# Revit family: 500_Slenderline_Sliding_Window_XXXX_Standard
name_source: partatom
category: Windows
revit_build: Autodesk Revit 2014 (Build: 20130308_1515(x64)
units: mm (PartAtom-declared; Revit-internal decimal feet)

## types (78) — shared parameters
Astragal Sash Gap = 1 mm  [stored 0.00328084 ft]
Centered In Wall = Yes
Custom Sash Width Side = 800 mm  [stored 2.62467 ft]
Default Sill Height = 800 mm  [stored 2.62467 ft]
Description = Slenderline Sliding Window
Equal Sash Width = Yes
Frame Thickness = 54 mm
Heavy Duty Handle = No
Heavy Duty Handle Gap = 27 mm
Heavy Duty Interlocker = No
Limit Sash Height Max = 1500 mm  [stored 4.92126 ft]
Limit Sash Height Min = 300 mm  [stored 0.984252 ft]
Limit Sash Width Max = 750 mm  [stored 2.46063 ft]
Limit Sash Width Min = 300 mm  [stored 0.984252 ft]
Limit Window Height Max = 1575 mm
Limit Window Height Min = 375 mm
Limit Window Width Max = 3024 mm
Limit Window Width Min = 1224 mm
Manufacturer = Crealco
Model = 500
Sash Frame Seal = 1 mm  [stored 0.00328084 ft]
Sash Rail Fore Aft Spacing = 2 mm  [stored 0.00656168 ft]
Standard Interlocker = Yes
URL = www.crealco.co.za
Wall Closure = By host
zero-valued in all types: Custom Frame Offset From Exterior, Is Heavy Duty Handle, Is Heavy Duty Mullion

## per-type parameters (varying)
| type | Area Middle Sash Glazing | Area Side Sash Glazing | Clearvue SHGC Value | Clearvue U Value | Custom Windload | Custom Window Height | Custom Window Width | Energy Advantage SHGC Value | Energy Advantage U Value | Height | Intruderprufe LowE SHGC Value | Intruderprufe LowE U Value | Intruderprufe SHGC Value | Intruderprufe U Value | Limit Sash Width Side Max | Limit Sash Width Side Min | Max Pane Area | Sash Height | Sash Width Middle | Sash Width Sides | Width | Windload Design |
| 500SW-1206XXXX-1000Pa | 0.12 m² | 0.12 m² | 0.535 | 5.67 | 1000 mm  [stored 3.28084 ft] | 590 mm  [stored 1.9357 ft] | 1190 mm  [stored 3.9042 ft] | 0.479 | 4.55 | 590 mm  [stored 1.9357 ft] | 0.406 | 4.29 | 0.508 | 5.53 | 300 mm  [stored 0.984252 ft] | 300 mm  [stored 0.984252 ft] | 0.12 m² | 515 mm | 300 mm  [stored 0.984252 ft] | 300 mm  [stored 0.984252 ft] | 1224 mm | 1000 mm  [stored 3.28084 ft] |
| 500SW-1506XXXX-1000Pa | 0.15 m² | 0.15 m² | 0.522 | 5.78 | 1000 mm  [stored 3.28084 ft] | 590 mm  [stored 1.9357 ft] | 1490 mm  [stored 4.88845 ft] | 0.495 | 4.57 | 590 mm  [stored 1.9357 ft] | 0.419 | 4.38 | 0.524 | 5.65 | 433 mm | 300 mm  [stored 0.984252 ft] | 0.15 m² | 515 mm | 367 mm | 367 mm | 1490 mm  [stored 4.88845 ft] | 1000 mm  [stored 3.28084 ft] |
| 500SW-1806XXXX-1000Pa | 0.18 m² | 0.18 m² | 0.564 | 5.86 | 1000 mm  [stored 3.28084 ft] | 590 mm  [stored 1.9357 ft] | 1790 mm  [stored 5.8727 ft] | 0.506 | 4.59 | 590 mm  [stored 1.9357 ft] | 0.429 | 4.43 | 0.536 | 5.72 | 583 mm | 300 mm  [stored 0.984252 ft] | 0.18 m² | 515 mm | 442 mm | 442 mm | 1790 mm  [stored 5.8727 ft] | 1000 mm  [stored 3.28084 ft] |
| 500SW-2106XXXX-1000Pa | 0.22 m² | 0.22 m² | 0.573 | 5.91 | 1000 mm  [stored 3.28084 ft] | 590 mm  [stored 1.9357 ft] | 2090 mm  [stored 6.85696 ft] | 0.513 | 4.61 | 590 mm  [stored 1.9357 ft] | 0.435 | 4.48 | 0.544 | 5.78 | 733 mm | 300 mm  [stored 0.984252 ft] | 0.22 m² | 515 mm | 517 mm | 517 mm | 2090 mm  [stored 6.85696 ft] | 1000 mm  [stored 3.28084 ft] |
| 500SW-2406XXXX-1000Pa | 0.25 m² | 0.25 m² | 0.579 | 5.95 | 1000 mm  [stored 3.28084 ft] | 590 mm  [stored 1.9357 ft] | 2390 mm  [stored 7.84121 ft] | 0.519 | 4.61 | 590 mm  [stored 1.9357 ft] | 0.44 | 4.51 | 0.55 | 5.82 | 750 mm  [stored 2.46063 ft] | 433 mm | 0.25 m² | 515 mm | 592 mm | 592 mm | 2390 mm  [stored 7.84121 ft] | 1000 mm  [stored 3.28084 ft] |
| 500SW-2706XXXX-1000Pa | 0.28 m² | 0.28 m² | 0.584 | 5.99 | 1000 mm  [stored 3.28084 ft] | 590 mm  [stored 1.9357 ft] | 2690 mm  [stored 8.82546 ft] | 0.523 | 4.62 | 590 mm  [stored 1.9357 ft] | 0.443 | 4.53 | 0.554 | 5.85 | 750 mm  [stored 2.46063 ft] | 583 mm | 0.28 m² | 515 mm | 667 mm | 667 mm | 2690 mm  [stored 8.82546 ft] | 1000 mm  [stored 3.28084 ft] |
| 500SW-3006XXXX-1000Pa | 0.32 m² | 0.32 m² | 0.588 | 6.01 | 1000 mm  [stored 3.28084 ft] | 590 mm  [stored 1.9357 ft] | 2990 mm  [stored 9.80971 ft] | 0.527 | 4.63 | 590 mm  [stored 1.9357 ft] | 0.47 | 4.56 | 0.588 | 5.88 | 750 mm  [stored 2.46063 ft] | 733 mm | 0.32 m² | 515 mm | 742 mm | 742 mm | 2990 mm  [stored 9.80971 ft] | 1000 mm  [stored 3.28084 ft] |
| 500SW-1209XXXX-1000Pa | 0.2 m² | 0.2 m² | 0.6 | 5.59 | 1000 mm  [stored 3.28084 ft] | 890 mm  [stored 2.91995 ft] | 1190 mm  [stored 3.9042 ft] | 0.538 | 4.33 | 890 mm  [stored 2.91995 ft] | 0.456 | 4.22 | 0.57 | 5.44 | 300 mm  [stored 0.984252 ft] | 300 mm  [stored 0.984252 ft] | 0.2 m² | 815 mm | 300 mm  [stored 0.984252 ft] | 300 mm  [stored 0.984252 ft] | 1224 mm | 1000 mm  [stored 3.28084 ft] |
| 500SW-1509XXXX-1000Pa | 0.25 m² | 0.25 m² | 0.62 | 5.69 | 1000 mm  [stored 3.28084 ft] | 890 mm  [stored 2.91995 ft] | 1490 mm  [stored 4.88845 ft] | 0.555 | 4.33 | 890 mm  [stored 2.91995 ft] | 0.471 | 4.3 | 0.589 | 5.55 | 433 mm | 300 mm  [stored 0.984252 ft] | 0.25 m² | 815 mm | 367 mm | 367 mm | 1490 mm  [stored 4.88845 ft] | 1000 mm  [stored 3.28084 ft] |
| 500SW-1809XXXX-1000Pa | 0.31 m² | 0.31 m² | 0.634 | 5.76 | 1000 mm  [stored 3.28084 ft] | 890 mm  [stored 2.91995 ft] | 1790 mm  [stored 5.8727 ft] | 0.567 | 4.33 | 890 mm  [stored 2.91995 ft] | 0.481 | 4.36 | 0.601 | 5.63 | 583 mm | 300 mm  [stored 0.984252 ft] | 0.31 m² | 815 mm | 442 mm | 442 mm | 1790 mm  [stored 5.8727 ft] | 1000 mm  [stored 3.28084 ft] |
| 500SW-2109XXXX-1000Pa | 0.36 m² | 0.36 m² | 0.643 | 5.81 | 1000 mm  [stored 3.28084 ft] | 890 mm  [stored 2.91995 ft] | 2090 mm  [stored 6.85696 ft] | 0.576 | 4.34 | 890 mm  [stored 2.91995 ft] | 0.488 | 4.4 | 0.61 | 5.68 | 733 mm | 300 mm  [stored 0.984252 ft] | 0.36 m² | 815 mm | 517 mm | 517 mm | 2090 mm  [stored 6.85696 ft] | 1000 mm  [stored 3.28084 ft] |
| 500SW-2409XXXX-1000Pa | 0.42 m² | 0.42 m² | 0.65 | 5.85 | 1000 mm  [stored 3.28084 ft] | 890 mm  [stored 2.91995 ft] | 2390 mm  [stored 7.84121 ft] | 0.582 | 4.34 | 890 mm  [stored 2.91995 ft] | 0.494 | 4.43 | 0.617 | 5.72 | 750 mm  [stored 2.46063 ft] | 433 mm | 0.42 m² | 815 mm | 592 mm | 592 mm | 2390 mm  [stored 7.84121 ft] | 1000 mm  [stored 3.28084 ft] |
| 500SW-2709XXXX-1000Pa | 0.47 m² | 0.47 m² | 0.656 | 5.88 | 1000 mm  [stored 3.28084 ft] | 890 mm  [stored 2.91995 ft] | 2690 mm  [stored 8.82546 ft] | 0.587 | 4.34 | 890 mm  [stored 2.91995 ft] | 0.498 | 4.46 | 0.622 | 5.75 | 750 mm  [stored 2.46063 ft] | 583 mm | 0.47 m² | 815 mm | 667 mm | 667 mm | 2690 mm  [stored 8.82546 ft] | 1000 mm  [stored 3.28084 ft] |
| 500SW-3009XXXX-1000Pa | 0.53 m² | 0.53 m² | 0.66 | 5.91 | 1000 mm  [stored 3.28084 ft] | 890 mm  [stored 2.91995 ft] | 2990 mm  [stored 9.80971 ft] | 0.591 | 4.34 | 890 mm  [stored 2.91995 ft] | 0.501 | 4.47 | 0.626 | 5.77 | 750 mm  [stored 2.46063 ft] | 733 mm | 0.53 m² | 815 mm | 742 mm | 742 mm | 2990 mm  [stored 9.80971 ft] | 1000 mm  [stored 3.28084 ft] |
| 500SW-1212XXXX-1000Pa | 0.28 m² | 0.28 m² | 0.633 | 5.55 | 1000 mm  [stored 3.28084 ft] | 1190 mm  [stored 3.9042 ft] | 1190 mm  [stored 3.9042 ft] | 0.567 | 4.22 | 1190 mm  [stored 3.9042 ft] | 0.481 | 4.19 | 0.601 | 5.4 | 300 mm  [stored 0.984252 ft] | 300 mm  [stored 0.984252 ft] | 0.28 m² | 1115 mm | 300 mm  [stored 0.984252 ft] | 300 mm  [stored 0.984252 ft] | 1224 mm | 1000 mm  [stored 3.28084 ft] |
| 500SW-1512XXXX-1000Pa | 0.35 m² | 0.35 m² | 0.654 | 5.65 | 1000 mm  [stored 3.28084 ft] | 1190 mm  [stored 3.9042 ft] | 1490 mm  [stored 4.88845 ft] | 0.585 | 4.21 | 1190 mm  [stored 3.9042 ft] | 0.497 | 4.27 | 0.621 | 5.51 | 433 mm | 300 mm  [stored 0.984252 ft] | 0.35 m² | 1115 mm | 367 mm | 367 mm | 1490 mm  [stored 4.88845 ft] | 1000 mm  [stored 3.28084 ft] |
| 500SW-1812XXXX-1000Pa | 0.43 m² | 0.43 m² | 0.668 | 5.72 | 1000 mm  [stored 3.28084 ft] | 1190 mm  [stored 3.9042 ft] | 1790 mm  [stored 5.8727 ft] | 0.598 | 4.21 | 1190 mm  [stored 3.9042 ft] | 0.507 | 4.33 | 0.634 | 5.58 | 583 mm | 300 mm  [stored 0.984252 ft] | 0.43 m² | 1115 mm | 442 mm | 442 mm | 1790 mm  [stored 5.8727 ft] | 1000 mm  [stored 3.28084 ft] |
| 500SW-2112XXXX-1000Pa | 0.51 m² | 0.51 m² | 0.678 | 5.77 | 1000 mm  [stored 3.28084 ft] | 1190 mm  [stored 3.9042 ft] | 2090 mm  [stored 6.85696 ft] | 0.606 | 4.2 | 1190 mm  [stored 3.9042 ft] | 0.514 | 4.36 | 0.643 | 5.63 | 733 mm | 300 mm  [stored 0.984252 ft] | 0.51 m² | 1115 mm | 517 mm | 517 mm | 2090 mm  [stored 6.85696 ft] | 1000 mm  [stored 3.28084 ft] |
| 500SW-2412XXXX-1000Pa | 0.59 m² | 0.59 m² | 0.686 | 5.8 | 1000 mm  [stored 3.28084 ft] | 1190 mm  [stored 3.9042 ft] | 2390 mm  [stored 7.84121 ft] | 0.613 | 4.2 | 1190 mm  [stored 3.9042 ft] | 0.52 | 4.4 | 0.65 | 5.67 | 750 mm  [stored 2.46063 ft] | 433 mm | 0.59 m² | 1115 mm | 592 mm | 592 mm | 2390 mm  [stored 7.84121 ft] | 1000 mm  [stored 3.28084 ft] |
| 500SW-2712XXXX-1000Pa | 0.66 m² | 0.66 m² | 0.691 | 5.83 | 1000 mm  [stored 3.28084 ft] | 1190 mm  [stored 3.9042 ft] | 2690 mm  [stored 8.82546 ft] | 0.618 | 4.2 | 1190 mm  [stored 3.9042 ft] | 0.525 | 4.41 | 0.656 | 5.69 | 750 mm  [stored 2.46063 ft] | 583 mm | 0.66 m² | 1115 mm | 667 mm | 667 mm | 2690 mm  [stored 8.82546 ft] | 1000 mm  [stored 3.28084 ft] |
| 500SW-3012XXXX-1000Pa | 0.74 m² | 0.74 m² | 0.696 | 5.85 | 1000 mm  [stored 3.28084 ft] | 1190 mm  [stored 3.9042 ft] | 2990 mm  [stored 9.80971 ft] | 0.622 | 4.2 | 1190 mm  [stored 3.9042 ft] | 0.528 | 4.43 | 0.66 | 5.72 | 750 mm  [stored 2.46063 ft] | 733 mm | 0.74 m² | 1115 mm | 742 mm | 742 mm | 2990 mm  [stored 9.80971 ft] | 1000 mm  [stored 3.28084 ft] |
| 500SW-1215XXXX-1000Pa | 0.36 m² | 0.36 m² | 0.653 | 5.52 | 1000 mm  [stored 3.28084 ft] | 1490 mm  [stored 4.88845 ft] | 1190 mm  [stored 3.9042 ft] | 0.584 | 4.15 | 1490 mm  [stored 4.88845 ft] | 0.495 | 4.17 | 0.619 | 5.38 | 300 mm  [stored 0.984252 ft] | 300 mm  [stored 0.984252 ft] | 0.36 m² | 1415 mm | 300 mm  [stored 0.984252 ft] | 300 mm  [stored 0.984252 ft] | 1224 mm | 1000 mm  [stored 3.28084 ft] |
| 500SW-1515XXXX-1000Pa | 0.45 m² | 0.45 m² | 0.674 | 5.62 | 1000 mm  [stored 3.28084 ft] | 1490 mm  [stored 4.88845 ft] | 1490 mm  [stored 4.88845 ft] | 0.603 | 4.14 | 1490 mm  [stored 4.88845 ft] | 0.512 | 4.25 | 0.64 | 5.48 | 433 mm | 300 mm  [stored 0.984252 ft] | 0.45 m² | 1415 mm | 367 mm | 367 mm | 1490 mm  [stored 4.88845 ft] | 1000 mm  [stored 3.28084 ft] |
| 500SW-1815XXXX-1000Pa | 0.55 m² | 0.55 m² | 0.689 | 5.69 | 1000 mm  [stored 3.28084 ft] | 1490 mm  [stored 4.88845 ft] | 1790 mm  [stored 5.8727 ft] | 0.616 | 4.13 | 1490 mm  [stored 4.88845 ft] | 0.522 | 4.3 | 0.653 | 5.55 | 583 mm | 300 mm  [stored 0.984252 ft] | 0.55 m² | 1415 mm | 442 mm | 442 mm | 1790 mm  [stored 5.8727 ft] | 1000 mm  [stored 3.28084 ft] |
| 500SW-2115XXXX-1000Pa | 0.65 m² | 0.65 m² | 0.699 | 5.74 | 1000 mm  [stored 3.28084 ft] | 1490 mm  [stored 4.88845 ft] | 2090 mm  [stored 6.85696 ft] | 0.625 | 4.12 | 1490 mm  [stored 4.88845 ft] | 0.53 | 4.34 | 0.663 | 5.6 | 733 mm | 300 mm  [stored 0.984252 ft] | 0.65 m² | 1415 mm | 517 mm | 517 mm | 2090 mm  [stored 6.85696 ft] | 1000 mm  [stored 3.28084 ft] |
| 500SW-2415XXXX-1000Pa | 0.75 m² | 0.75 m² | 0.707 | 5.77 | 1000 mm  [stored 3.28084 ft] | 1490 mm  [stored 4.88845 ft] | 2390 mm  [stored 7.84121 ft] | 0.632 | 4.12 | 1490 mm  [stored 4.88845 ft] | 0.536 | 4.36 | 0.67 | 5.63 | 750 mm  [stored 2.46063 ft] | 433 mm | 0.75 m² | 1415 mm | 592 mm | 592 mm | 2390 mm  [stored 7.84121 ft] | 1000 mm  [stored 3.28084 ft] |
| 500SW-2715XXXX-1000Pa | 0.85 m² | 0.85 m² | 0.713 | 5.8 | 1000 mm  [stored 3.28084 ft] | 1490 mm  [stored 4.88845 ft] | 2690 mm  [stored 8.82546 ft] | 0.637 | 4.12 | 1490 mm  [stored 4.88845 ft] | 0.541 | 4.39 | 0.676 | 5.66 | 750 mm  [stored 2.46063 ft] | 583 mm | 0.85 m² | 1415 mm | 667 mm | 667 mm | 2690 mm  [stored 8.82546 ft] | 1000 mm  [stored 3.28084 ft] |
| 500SW-3015XXXX-1000Pa | 0.96 m² | 0.96 m² | 0.717 | 5.82 | 1000 mm  [stored 3.28084 ft] | 1490 mm  [stored 4.88845 ft] | 2990 mm  [stored 9.80971 ft] | 0.641 | 4.11 | 1490 mm  [stored 4.88845 ft] | 0.544 | 4.41 | 0.68 | 5.69 | 750 mm  [stored 2.46063 ft] | 733 mm | 0.96 m² | 1415 mm | 742 mm | 742 mm | 2990 mm  [stored 9.80971 ft] | 1000 mm  [stored 3.28084 ft] |
| 500SW-1206XXXX-1500Pa | 0.12 m² | 0.12 m² | 0.535 | 5.67 | 1500 mm  [stored 4.92126 ft] | 590 mm  [stored 1.9357 ft] | 1190 mm  [stored 3.9042 ft] | 0.479 | 4.55 | 590 mm  [stored 1.9357 ft] | 0.406 | 4.29 | 0.508 | 5.53 | 300 mm  [stored 0.984252 ft] | 300 mm  [stored 0.984252 ft] | 0.12 m² | 515 mm | 300 mm  [stored 0.984252 ft] | 300 mm  [stored 0.984252 ft] | 1224 mm | 1500 mm  [stored 4.92126 ft] |
| 500SW-1206XXXX-2000Pa | 0.12 m² | 0.12 m² | 0.535 | 5.67 | 2000 mm  [stored 6.56168 ft] | 590 mm  [stored 1.9357 ft] | 1190 mm  [stored 3.9042 ft] | 0.479 | 4.55 | 590 mm  [stored 1.9357 ft] | 0.406 | 4.29 | 0.508 | 5.53 | 300 mm  [stored 0.984252 ft] | 300 mm  [stored 0.984252 ft] | 0.12 m² | 515 mm | 300 mm  [stored 0.984252 ft] | 300 mm  [stored 0.984252 ft] | 1224 mm | 2000 mm  [stored 6.56168 ft] |
| 500SW-1209XXXX-1500Pa | 0.2 m² | 0.2 m² | 0.6 | 5.59 | 1500 mm  [stored 4.92126 ft] | 890 mm  [stored 2.91995 ft] | 1190 mm  [stored 3.9042 ft] | 0.538 | 4.33 | 890 mm  [stored 2.91995 ft] | 0.456 | 4.22 | 0.57 | 5.44 | 300 mm  [stored 0.984252 ft] | 300 mm  [stored 0.984252 ft] | 0.2 m² | 815 mm | 300 mm  [stored 0.984252 ft] | 300 mm  [stored 0.984252 ft] | 1224 mm | 1500 mm  [stored 4.92126 ft] |
| 500SW-1209XXXX-2000Pa | 0.2 m² | 0.2 m² | 0.6 | 5.59 | 2000 mm  [stored 6.56168 ft] | 890 mm  [stored 2.91995 ft] | 1190 mm  [stored 3.9042 ft] | 0.538 | 4.33 | 890 mm  [stored 2.91995 ft] | 0.456 | 4.22 | 0.57 | 5.44 | 300 mm  [stored 0.984252 ft] | 300 mm  [stored 0.984252 ft] | 0.2 m² | 815 mm | 300 mm  [stored 0.984252 ft] | 300 mm  [stored 0.984252 ft] | 1224 mm | 2000 mm  [stored 6.56168 ft] |
| 500SW-1212XXXX-1500Pa | 0.28 m² | 0.28 m² | 0.633 | 5.55 | 1500 mm  [stored 4.92126 ft] | 1190 mm  [stored 3.9042 ft] | 1190 mm  [stored 3.9042 ft] | 0.567 | 4.22 | 1190 mm  [stored 3.9042 ft] | 0.481 | 4.19 | 0.601 | 5.4 | 300 mm  [stored 0.984252 ft] | 300 mm  [stored 0.984252 ft] | 0.28 m² | 1115 mm | 300 mm  [stored 0.984252 ft] | 300 mm  [stored 0.984252 ft] | 1224 mm | 1500 mm  [stored 4.92126 ft] |
| 500SW-1212XXXX-2000Pa | 0.28 m² | 0.28 m² | 0.633 | 5.55 | 2000 mm  [stored 6.56168 ft] | 1190 mm  [stored 3.9042 ft] | 1190 mm  [stored 3.9042 ft] | 0.567 | 4.22 | 1190 mm  [stored 3.9042 ft] | 0.481 | 4.19 | 0.601 | 5.4 | 300 mm  [stored 0.984252 ft] | 300 mm  [stored 0.984252 ft] | 0.28 m² | 1115 mm | 300 mm  [stored 0.984252 ft] | 300 mm  [stored 0.984252 ft] | 1224 mm | 2000 mm  [stored 6.56168 ft] |
| 500SW-1215XXXX-1500Pa | 0.36 m² | 0.36 m² | 0.653 | 5.52 | 1500 mm  [stored 4.92126 ft] | 1490 mm  [stored 4.88845 ft] | 1190 mm  [stored 3.9042 ft] | 0.584 | 4.15 | 1490 mm  [stored 4.88845 ft] | 0.495 | 4.17 | 0.619 | 5.38 | 300 mm  [stored 0.984252 ft] | 300 mm  [stored 0.984252 ft] | 0.36 m² | 1415 mm | 300 mm  [stored 0.984252 ft] | 300 mm  [stored 0.984252 ft] | 1224 mm | 1500 mm  [stored 4.92126 ft] |
| 500SW-1215XXXX-2000Pa | 0.36 m² | 0.36 m² | 0.653 | 5.52 | 2000 mm  [stored 6.56168 ft] | 1490 mm  [stored 4.88845 ft] | 1190 mm  [stored 3.9042 ft] | 0.584 | 4.15 | 1490 mm  [stored 4.88845 ft] | 0.495 | 4.17 | 0.619 | 5.38 | 300 mm  [stored 0.984252 ft] | 300 mm  [stored 0.984252 ft] | 0.36 m² | 1415 mm | 300 mm  [stored 0.984252 ft] | 300 mm  [stored 0.984252 ft] | 1224 mm | 2000 mm  [stored 6.56168 ft] |
| 500SW-1506XXXX-1500Pa | 0.15 m² | 0.15 m² | 0.522 | 5.78 | 1500 mm  [stored 4.92126 ft] | 590 mm  [stored 1.9357 ft] | 1490 mm  [stored 4.88845 ft] | 0.495 | 4.57 | 590 mm  [stored 1.9357 ft] | 0.419 | 4.38 | 0.524 | 5.65 | 433 mm | 300 mm  [stored 0.984252 ft] | 0.15 m² | 515 mm | 367 mm | 367 mm | 1490 mm  [stored 4.88845 ft] | 1500 mm  [stored 4.92126 ft] |
| 500SW-1506XXXX-2000Pa | 0.15 m² | 0.15 m² | 0.522 | 5.78 | 2000 mm  [stored 6.56168 ft] | 590 mm  [stored 1.9357 ft] | 1490 mm  [stored 4.88845 ft] | 0.495 | 4.57 | 590 mm  [stored 1.9357 ft] | 0.419 | 4.38 | 0.524 | 5.65 | 433 mm | 300 mm  [stored 0.984252 ft] | 0.15 m² | 515 mm | 367 mm | 367 mm | 1490 mm  [stored 4.88845 ft] | 2000 mm  [stored 6.56168 ft] |
| 500SW-1509XXXX-1500Pa | 0.25 m² | 0.25 m² | 0.62 | 5.69 | 1500 mm  [stored 4.92126 ft] | 890 mm  [stored 2.91995 ft] | 1490 mm  [stored 4.88845 ft] | 0.555 | 4.33 | 890 mm  [stored 2.91995 ft] | 0.471 | 4.3 | 0.589 | 5.55 | 433 mm | 300 mm  [stored 0.984252 ft] | 0.25 m² | 815 mm | 367 mm | 367 mm | 1490 mm  [stored 4.88845 ft] | 1500 mm  [stored 4.92126 ft] |
| 500SW-1509XXXX-2000Pa | 0.25 m² | 0.25 m² | 0.62 | 5.69 | 2000 mm  [stored 6.56168 ft] | 890 mm  [stored 2.91995 ft] | 1490 mm  [stored 4.88845 ft] | 0.555 | 4.33 | 890 mm  [stored 2.91995 ft] | 0.471 | 4.3 | 0.589 | 5.55 | 433 mm | 300 mm  [stored 0.984252 ft] | 0.25 m² | 815 mm | 367 mm | 367 mm | 1490 mm  [stored 4.88845 ft] | 2000 mm  [stored 6.56168 ft] |
| 500SW-1512XXXX-1500Pa | 0.35 m² | 0.35 m² | 0.654 | 5.65 | 1500 mm  [stored 4.92126 ft] | 1190 mm  [stored 3.9042 ft] | 1490 mm  [stored 4.88845 ft] | 0.585 | 4.21 | 1190 mm  [stored 3.9042 ft] | 0.497 | 4.27 | 0.621 | 5.51 | 433 mm | 300 mm  [stored 0.984252 ft] | 0.35 m² | 1115 mm | 367 mm | 367 mm | 1490 mm  [stored 4.88845 ft] | 1500 mm  [stored 4.92126 ft] |
| 500SW-1512XXXX-2000Pa | 0.35 m² | 0.35 m² | 0.654 | 5.65 | 2000 mm  [stored 6.56168 ft] | 1190 mm  [stored 3.9042 ft] | 1490 mm  [stored 4.88845 ft] | 0.585 | 4.21 | 1190 mm  [stored 3.9042 ft] | 0.497 | 4.27 | 0.621 | 5.51 | 433 mm | 300 mm  [stored 0.984252 ft] | 0.35 m² | 1115 mm | 367 mm | 367 mm | 1490 mm  [stored 4.88845 ft] | 2000 mm  [stored 6.56168 ft] |
| 500SW-1515XXXX-1500Pa | 0.45 m² | 0.45 m² | 0.674 | 5.62 | 1500 mm  [stored 4.92126 ft] | 1490 mm  [stored 4.88845 ft] | 1490 mm  [stored 4.88845 ft] | 0.603 | 4.14 | 1490 mm  [stored 4.88845 ft] | 0.512 | 4.25 | 0.64 | 5.48 | 433 mm | 300 mm  [stored 0.984252 ft] | 0.45 m² | 1415 mm | 367 mm | 367 mm | 1490 mm  [stored 4.88845 ft] | 1500 mm  [stored 4.92126 ft] |
| 500SW-1515XXXX-2000Pa | 0.45 m² | 0.45 m² | 0.674 | 5.62 | 2000 mm  [stored 6.56168 ft] | 1490 mm  [stored 4.88845 ft] | 1490 mm  [stored 4.88845 ft] | 0.603 | 4.14 | 1490 mm  [stored 4.88845 ft] | 0.512 | 4.25 | 0.64 | 5.48 | 433 mm | 300 mm  [stored 0.984252 ft] | 0.45 m² | 1415 mm | 367 mm | 367 mm | 1490 mm  [stored 4.88845 ft] | 2000 mm  [stored 6.56168 ft] |
| 500SW-1806XXXX-1500Pa | 0.18 m² | 0.18 m² | 0.564 | 5.86 | 1500 mm  [stored 4.92126 ft] | 590 mm  [stored 1.9357 ft] | 1790 mm  [stored 5.8727 ft] | 0.506 | 4.59 | 590 mm  [stored 1.9357 ft] | 0.429 | 4.43 | 0.536 | 5.72 | 583 mm | 300 mm  [stored 0.984252 ft] | 0.18 m² | 515 mm | 442 mm | 442 mm | 1790 mm  [stored 5.8727 ft] | 1500 mm  [stored 4.92126 ft] |
| 500SW-1806XXXX-2000Pa | 0.18 m² | 0.18 m² | 0.564 | 5.86 | 2000 mm  [stored 6.56168 ft] | 590 mm  [stored 1.9357 ft] | 1790 mm  [stored 5.8727 ft] | 0.506 | 4.59 | 590 mm  [stored 1.9357 ft] | 0.429 | 4.43 | 0.536 | 5.72 | 583 mm | 300 mm  [stored 0.984252 ft] | 0.18 m² | 515 mm | 442 mm | 442 mm | 1790 mm  [stored 5.8727 ft] | 2000 mm  [stored 6.56168 ft] |
| 500SW-1809XXXX-1500Pa | 0.31 m² | 0.31 m² | 0.634 | 5.76 | 1500 mm  [stored 4.92126 ft] | 890 mm  [stored 2.91995 ft] | 1790 mm  [stored 5.8727 ft] | 0.567 | 4.33 | 890 mm  [stored 2.91995 ft] | 0.481 | 4.36 | 0.601 | 5.63 | 583 mm | 300 mm  [stored 0.984252 ft] | 0.31 m² | 815 mm | 442 mm | 442 mm | 1790 mm  [stored 5.8727 ft] | 1500 mm  [stored 4.92126 ft] |
| 500SW-1809XXXX-2000Pa | 0.31 m² | 0.31 m² | 0.634 | 5.76 | 2000 mm  [stored 6.56168 ft] | 890 mm  [stored 2.91995 ft] | 1790 mm  [stored 5.8727 ft] | 0.567 | 4.33 | 890 mm  [stored 2.91995 ft] | 0.481 | 4.36 | 0.601 | 5.63 | 583 mm | 300 mm  [stored 0.984252 ft] | 0.31 m² | 815 mm | 442 mm | 442 mm | 1790 mm  [stored 5.8727 ft] | 2000 mm  [stored 6.56168 ft] |
| 500SW-1812XXXX-1500Pa | 0.43 m² | 0.43 m² | 0.668 | 5.72 | 1500 mm  [stored 4.92126 ft] | 1190 mm  [stored 3.9042 ft] | 1790 mm  [stored 5.8727 ft] | 0.598 | 4.21 | 1190 mm  [stored 3.9042 ft] | 0.507 | 4.33 | 0.634 | 5.58 | 583 mm | 300 mm  [stored 0.984252 ft] | 0.43 m² | 1115 mm | 442 mm | 442 mm | 1790 mm  [stored 5.8727 ft] | 1500 mm  [stored 4.92126 ft] |
| 500SW-1812XXXX-2000Pa | 0.43 m² | 0.43 m² | 0.668 | 5.72 | 2000 mm  [stored 6.56168 ft] | 1190 mm  [stored 3.9042 ft] | 1790 mm  [stored 5.8727 ft] | 0.598 | 4.21 | 1190 mm  [stored 3.9042 ft] | 0.507 | 4.33 | 0.634 | 5.58 | 583 mm | 300 mm  [stored 0.984252 ft] | 0.43 m² | 1115 mm | 442 mm | 442 mm | 1790 mm  [stored 5.8727 ft] | 2000 mm  [stored 6.56168 ft] |
| 500SW-1815XXXX-1500Pa | 0.55 m² | 0.55 m² | 0.689 | 5.69 | 1500 mm  [stored 4.92126 ft] | 1490 mm  [stored 4.88845 ft] | 1790 mm  [stored 5.8727 ft] | 0.616 | 4.13 | 1490 mm  [stored 4.88845 ft] | 0.522 | 4.3 | 0.653 | 5.55 | 583 mm | 300 mm  [stored 0.984252 ft] | 0.55 m² | 1415 mm | 442 mm | 442 mm | 1790 mm  [stored 5.8727 ft] | 1500 mm  [stored 4.92126 ft] |
| 500SW-1815XXXX-2000Pa | 0.55 m² | 0.55 m² | 0.689 | 5.69 | 2000 mm  [stored 6.56168 ft] | 1490 mm  [stored 4.88845 ft] | 1790 mm  [stored 5.8727 ft] | 0.616 | 4.13 | 1490 mm  [stored 4.88845 ft] | 0.522 | 4.3 | 0.653 | 5.55 | 583 mm | 300 mm  [stored 0.984252 ft] | 0.55 m² | 1415 mm | 442 mm | 442 mm | 1790 mm  [stored 5.8727 ft] | 2000 mm  [stored 6.56168 ft] |
| 500SW-2106XXXX-1500Pa | 0.22 m² | 0.22 m² | 0.573 | 5.91 | 1500 mm  [stored 4.92126 ft] | 590 mm  [stored 1.9357 ft] | 2090 mm  [stored 6.85696 ft] | 0.513 | 4.61 | 590 mm  [stored 1.9357 ft] | 0.435 | 4.48 | 0.544 | 5.78 | 733 mm | 300 mm  [stored 0.984252 ft] | 0.22 m² | 515 mm | 517 mm | 517 mm | 2090 mm  [stored 6.85696 ft] | 1500 mm  [stored 4.92126 ft] |
| 500SW-2106XXXX-2000Pa | 0.22 m² | 0.22 m² | 0.573 | 5.91 | 2000 mm  [stored 6.56168 ft] | 590 mm  [stored 1.9357 ft] | 2090 mm  [stored 6.85696 ft] | 0.513 | 4.61 | 590 mm  [stored 1.9357 ft] | 0.435 | 4.48 | 0.544 | 5.78 | 733 mm | 300 mm  [stored 0.984252 ft] | 0.22 m² | 515 mm | 517 mm | 517 mm | 2090 mm  [stored 6.85696 ft] | 2000 mm  [stored 6.56168 ft] |
| 500SW-2109XXXX-1500Pa | 0.36 m² | 0.36 m² | 0.643 | 5.81 | 1500 mm  [stored 4.92126 ft] | 890 mm  [stored 2.91995 ft] | 2090 mm  [stored 6.85696 ft] | 0.576 | 4.34 | 890 mm  [stored 2.91995 ft] | 0.488 | 4.4 | 0.61 | 5.68 | 733 mm | 300 mm  [stored 0.984252 ft] | 0.36 m² | 815 mm | 517 mm | 517 mm | 2090 mm  [stored 6.85696 ft] | 1500 mm  [stored 4.92126 ft] |
| 500SW-2109XXXX-2000Pa | 0.36 m² | 0.36 m² | 0.643 | 5.81 | 2000 mm  [stored 6.56168 ft] | 890 mm  [stored 2.91995 ft] | 2090 mm  [stored 6.85696 ft] | 0.576 | 4.34 | 890 mm  [stored 2.91995 ft] | 0.488 | 4.4 | 0.61 | 5.68 | 733 mm | 300 mm  [stored 0.984252 ft] | 0.36 m² | 815 mm | 517 mm | 517 mm | 2090 mm  [stored 6.85696 ft] | 2000 mm  [stored 6.56168 ft] |
| 500SW-2112XXXX-1500Pa | 0.51 m² | 0.51 m² | 0.678 | 5.77 | 1500 mm  [stored 4.92126 ft] | 1190 mm  [stored 3.9042 ft] | 2090 mm  [stored 6.85696 ft] | 0.606 | 4.2 | 1190 mm  [stored 3.9042 ft] | 0.514 | 4.36 | 0.643 | 5.63 | 733 mm | 300 mm  [stored 0.984252 ft] | 0.51 m² | 1115 mm | 517 mm | 517 mm | 2090 mm  [stored 6.85696 ft] | 1500 mm  [stored 4.92126 ft] |
| 500SW-2112XXXX-2000Pa | 0.51 m² | 0.51 m² | 0.678 | 5.77 | 2000 mm  [stored 6.56168 ft] | 1190 mm  [stored 3.9042 ft] | 2090 mm  [stored 6.85696 ft] | 0.606 | 4.2 | 1190 mm  [stored 3.9042 ft] | 0.514 | 4.36 | 0.643 | 5.63 | 733 mm | 300 mm  [stored 0.984252 ft] | 0.51 m² | 1115 mm | 517 mm | 517 mm | 2090 mm  [stored 6.85696 ft] | 2000 mm  [stored 6.56168 ft] |
| 500SW-2115XXXX-1500Pa | 0.65 m² | 0.65 m² | 0.699 | 5.74 | 1500 mm  [stored 4.92126 ft] | 1490 mm  [stored 4.88845 ft] | 2090 mm  [stored 6.85696 ft] | 0.625 | 4.12 | 1490 mm  [stored 4.88845 ft] | 0.53 | 4.34 | 0.663 | 5.6 | 733 mm | 300 mm  [stored 0.984252 ft] | 0.65 m² | 1415 mm | 517 mm | 517 mm | 2090 mm  [stored 6.85696 ft] | 1500 mm  [stored 4.92126 ft] |
| 500SW-2406XXXX-1500Pa | 0.25 m² | 0.25 m² | 0.579 | 5.95 | 1500 mm  [stored 4.92126 ft] | 590 mm  [stored 1.9357 ft] | 2390 mm  [stored 7.84121 ft] | 0.519 | 4.61 | 590 mm  [stored 1.9357 ft] | 0.44 | 4.51 | 0.55 | 5.82 | 750 mm  [stored 2.46063 ft] | 433 mm | 0.25 m² | 515 mm | 592 mm | 592 mm | 2390 mm  [stored 7.84121 ft] | 1500 mm  [stored 4.92126 ft] |
| 500SW-2406XXXX-2000Pa | 0.25 m² | 0.25 m² | 0.579 | 5.95 | 2000 mm  [stored 6.56168 ft] | 590 mm  [stored 1.9357 ft] | 2390 mm  [stored 7.84121 ft] | 0.519 | 4.61 | 590 mm  [stored 1.9357 ft] | 0.44 | 4.51 | 0.55 | 5.82 | 750 mm  [stored 2.46063 ft] | 433 mm | 0.25 m² | 515 mm | 592 mm | 592 mm | 2390 mm  [stored 7.84121 ft] | 2000 mm  [stored 6.56168 ft] |
| 500SW-2409XXXX-1500Pa | 0.42 m² | 0.42 m² | 0.65 | 5.85 | 1500 mm  [stored 4.92126 ft] | 890 mm  [stored 2.91995 ft] | 2390 mm  [stored 7.84121 ft] | 0.582 | 4.34 | 890 mm  [stored 2.91995 ft] | 0.494 | 4.43 | 0.617 | 5.72 | 750 mm  [stored 2.46063 ft] | 433 mm | 0.42 m² | 815 mm | 592 mm | 592 mm | 2390 mm  [stored 7.84121 ft] | 1500 mm  [stored 4.92126 ft] |
| 500SW-2409XXXX-2000Pa | 0.42 m² | 0.42 m² | 0.65 | 5.85 | 2000 mm  [stored 6.56168 ft] | 890 mm  [stored 2.91995 ft] | 2390 mm  [stored 7.84121 ft] | 0.582 | 4.34 | 890 mm  [stored 2.91995 ft] | 0.494 | 4.43 | 0.617 | 5.72 | 750 mm  [stored 2.46063 ft] | 433 mm | 0.42 m² | 815 mm | 592 mm | 592 mm | 2390 mm  [stored 7.84121 ft] | 2000 mm  [stored 6.56168 ft] |
| 500SW-2412XXXX-1500Pa | 0.59 m² | 0.59 m² | 0.686 | 5.8 | 1500 mm  [stored 4.92126 ft] | 1190 mm  [stored 3.9042 ft] | 2390 mm  [stored 7.84121 ft] | 0.613 | 4.2 | 1190 mm  [stored 3.9042 ft] | 0.52 | 4.4 | 0.65 | 5.67 | 750 mm  [stored 2.46063 ft] | 433 mm | 0.59 m² | 1115 mm | 592 mm | 592 mm | 2390 mm  [stored 7.84121 ft] | 1500 mm  [stored 4.92126 ft] |
| 500SW-2412XXXX-2000Pa | 0.59 m² | 0.59 m² | 0.686 | 5.8 | 2000 mm  [stored 6.56168 ft] | 1190 mm  [stored 3.9042 ft] | 2390 mm  [stored 7.84121 ft] | 0.613 | 4.2 | 1190 mm  [stored 3.9042 ft] | 0.52 | 4.4 | 0.65 | 5.67 | 750 mm  [stored 2.46063 ft] | 433 mm | 0.59 m² | 1115 mm | 592 mm | 592 mm | 2390 mm  [stored 7.84121 ft] | 2000 mm  [stored 6.56168 ft] |
| 500SW-2415XXXX-1500Pa | 0.75 m² | 0.75 m² | 0.707 | 5.77 | 1500 mm  [stored 4.92126 ft] | 1490 mm  [stored 4.88845 ft] | 2390 mm  [stored 7.84121 ft] | 0.632 | 4.12 | 1490 mm  [stored 4.88845 ft] | 0.536 | 4.36 | 0.67 | 5.63 | 750 mm  [stored 2.46063 ft] | 433 mm | 0.75 m² | 1415 mm | 592 mm | 592 mm | 2390 mm  [stored 7.84121 ft] | 1500 mm  [stored 4.92126 ft] |
| 500SW-2706XXXX-1500Pa | 0.28 m² | 0.28 m² | 0.584 | 5.99 | 1500 mm  [stored 4.92126 ft] | 590 mm  [stored 1.9357 ft] | 2690 mm  [stored 8.82546 ft] | 0.523 | 4.62 | 590 mm  [stored 1.9357 ft] | 0.443 | 4.53 | 0.554 | 5.85 | 750 mm  [stored 2.46063 ft] | 583 mm | 0.28 m² | 515 mm | 667 mm | 667 mm | 2690 mm  [stored 8.82546 ft] | 1500 mm  [stored 4.92126 ft] |
| 500SW-2706XXXX-2000Pa | 0.28 m² | 0.28 m² | 0.584 | 5.99 | 2000 mm  [stored 6.56168 ft] | 590 mm  [stored 1.9357 ft] | 2690 mm  [stored 8.82546 ft] | 0.523 | 4.62 | 590 mm  [stored 1.9357 ft] | 0.443 | 4.53 | 0.554 | 5.85 | 750 mm  [stored 2.46063 ft] | 583 mm | 0.28 m² | 515 mm | 667 mm | 667 mm | 2690 mm  [stored 8.82546 ft] | 2000 mm  [stored 6.56168 ft] |
| 500SW-2709XXXX-1500Pa | 0.47 m² | 0.47 m² | 0.656 | 5.88 | 1500 mm  [stored 4.92126 ft] | 890 mm  [stored 2.91995 ft] | 2690 mm  [stored 8.82546 ft] | 0.587 | 4.34 | 890 mm  [stored 2.91995 ft] | 0.498 | 4.46 | 0.622 | 5.75 | 750 mm  [stored 2.46063 ft] | 583 mm | 0.47 m² | 815 mm | 667 mm | 667 mm | 2690 mm  [stored 8.82546 ft] | 1500 mm  [stored 4.92126 ft] |
| 500SW-2709XXXX-2000Pa | 0.47 m² | 0.47 m² | 0.656 | 5.88 | 2000 mm  [stored 6.56168 ft] | 890 mm  [stored 2.91995 ft] | 2690 mm  [stored 8.82546 ft] | 0.587 | 4.34 | 890 mm  [stored 2.91995 ft] | 0.498 | 4.46 | 0.622 | 5.75 | 750 mm  [stored 2.46063 ft] | 583 mm | 0.47 m² | 815 mm | 667 mm | 667 mm | 2690 mm  [stored 8.82546 ft] | 2000 mm  [stored 6.56168 ft] |
| 500SW-2712XXXX-1500Pa | 0.66 m² | 0.66 m² | 0.691 | 5.83 | 1500 mm  [stored 4.92126 ft] | 1190 mm  [stored 3.9042 ft] | 2690 mm  [stored 8.82546 ft] | 0.618 | 4.2 | 1190 mm  [stored 3.9042 ft] | 0.525 | 4.41 | 0.656 | 5.69 | 750 mm  [stored 2.46063 ft] | 583 mm | 0.66 m² | 1115 mm | 667 mm | 667 mm | 2690 mm  [stored 8.82546 ft] | 1500 mm  [stored 4.92126 ft] |
| 500SW-2712XXXX-2000Pa | 0.66 m² | 0.66 m² | 0.691 | 5.83 | 2000 mm  [stored 6.56168 ft] | 1190 mm  [stored 3.9042 ft] | 2690 mm  [stored 8.82546 ft] | 0.618 | 4.2 | 1190 mm  [stored 3.9042 ft] | 0.525 | 4.41 | 0.656 | 5.69 | 750 mm  [stored 2.46063 ft] | 583 mm | 0.66 m² | 1115 mm | 667 mm | 667 mm | 2690 mm  [stored 8.82546 ft] | 2000 mm  [stored 6.56168 ft] |
| 500SW-3006XXXX-1500Pa | 0.32 m² | 0.32 m² | 0.588 | 6.01 | 1500 mm  [stored 4.92126 ft] | 590 mm  [stored 1.9357 ft] | 2990 mm  [stored 9.80971 ft] | 0.527 | 4.63 | 590 mm  [stored 1.9357 ft] | 0.47 | 4.56 | 0.588 | 5.88 | 750 mm  [stored 2.46063 ft] | 733 mm | 0.32 m² | 515 mm | 742 mm | 742 mm | 2990 mm  [stored 9.80971 ft] | 1500 mm  [stored 4.92126 ft] |
| 500SW-3006XXXX-2000Pa | 0.32 m² | 0.32 m² | 0.588 | 6.01 | 2000 mm  [stored 6.56168 ft] | 590 mm  [stored 1.9357 ft] | 2990 mm  [stored 9.80971 ft] | 0.527 | 4.63 | 590 mm  [stored 1.9357 ft] | 0.47 | 4.56 | 0.588 | 5.88 | 750 mm  [stored 2.46063 ft] | 733 mm | 0.32 m² | 515 mm | 742 mm | 742 mm | 2990 mm  [stored 9.80971 ft] | 2000 mm  [stored 6.56168 ft] |
| 500SW-3009XXXX-1500Pa | 0.53 m² | 0.53 m² | 0.66 | 5.91 | 1500 mm  [stored 4.92126 ft] | 890 mm  [stored 2.91995 ft] | 2990 mm  [stored 9.80971 ft] | 0.591 | 4.34 | 890 mm  [stored 2.91995 ft] | 0.501 | 4.47 | 0.626 | 5.77 | 750 mm  [stored 2.46063 ft] | 733 mm | 0.53 m² | 815 mm | 742 mm | 742 mm | 2990 mm  [stored 9.80971 ft] | 1500 mm  [stored 4.92126 ft] |
| 500SW-3009XXXX-2000Pa | 0.53 m² | 0.53 m² | 0.66 | 5.91 | 2000 mm  [stored 6.56168 ft] | 890 mm  [stored 2.91995 ft] | 2990 mm  [stored 9.80971 ft] | 0.591 | 4.34 | 890 mm  [stored 2.91995 ft] | 0.501 | 4.47 | 0.626 | 5.77 | 750 mm  [stored 2.46063 ft] | 733 mm | 0.53 m² | 815 mm | 742 mm | 742 mm | 2990 mm  [stored 9.80971 ft] | 2000 mm  [stored 6.56168 ft] |
| 500SW-3012XXXX-1500Pa | 0.74 m² | 0.74 m² | 0.696 | 5.85 | 1500 mm  [stored 4.92126 ft] | 1190 mm  [stored 3.9042 ft] | 2990 mm  [stored 9.80971 ft] | 0.622 | 4.2 | 1190 mm  [stored 3.9042 ft] | 0.528 | 4.43 | 0.66 | 5.72 | 750 mm  [stored 2.46063 ft] | 733 mm | 0.74 m² | 1115 mm | 742 mm | 742 mm | 2990 mm  [stored 9.80971 ft] | 1500 mm  [stored 4.92126 ft] |
| 500SW-3012XXXX-2000Pa | 0.74 m² | 0.74 m² | 0.696 | 5.85 | 2000 mm  [stored 6.56168 ft] | 1190 mm  [stored 3.9042 ft] | 2990 mm  [stored 9.80971 ft] | 0.622 | 4.2 | 1190 mm  [stored 3.9042 ft] | 0.528 | 4.43 | 0.66 | 5.72 | 750 mm  [stored 2.46063 ft] | 733 mm | 0.74 m² | 1115 mm | 742 mm | 742 mm | 2990 mm  [stored 9.80971 ft] | 2000 mm  [stored 6.56168 ft] |

note: [stored X ft] marks values corroborated as IEEE doubles in the binary element streams (Revit-internal decimal feet)

## geometry (parser evidence)
native form markers: Sweep x50
no freeform markers — native parametric forms only
